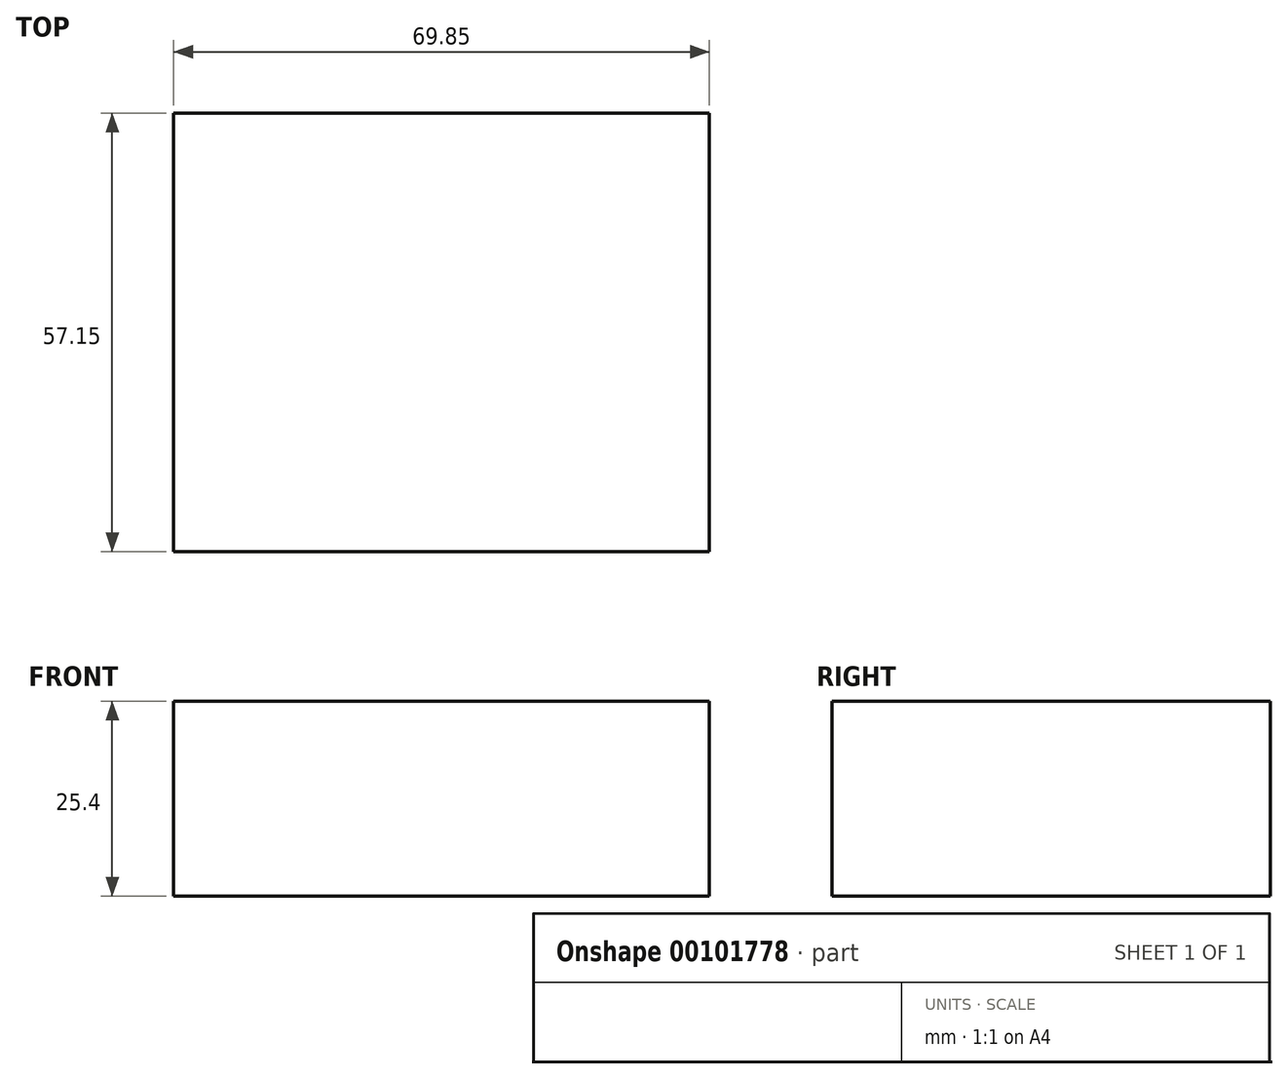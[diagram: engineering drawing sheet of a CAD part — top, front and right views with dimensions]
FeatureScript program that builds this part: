
annotation { "Feature Type Name" : "Feature", "Feature Type Description" : "" }
export const myFeature = defineFeature(function(context is Context, id is Id, definition is map)
    precondition{}
    {
        {
            var Q0;
            Q0=qCreatedBy(makeId("Front.planeOp"),FACE);
            var sketch = newSketch(context, id + "F0", { "sketchPlane" : qUnion([Q0])});
            skLineSegment(sketch, "E0.bottom", {"start": v(-23.12, 6.57) * mm, "end": v(46.73, 6.57) * mm});
            skLineSegment(sketch, "E0.top", {"start": v(-23.12, -18.83) * mm, "end": v(46.73, -18.83) * mm});
            skLineSegment(sketch, "E0.left", {"start": v(-23.12, 6.57) * mm, "end": v(-23.12, -18.83) * mm});
            skLineSegment(sketch, "E0.right", {"start": v(46.73, 6.57) * mm, "end": v(46.73, -18.83) * mm});
            skSolve(sketch);
        }
        {
            var Q0;
            Q0=makeQuery(id+"F0.imprint","IMPRINT",FACE,{"disambiguationData":[TD([[makeQuery(id+"F0.imprint","IMPRINT",EDGE,{"derivedFrom":sQuery(id+"F0.wireOp",EDGE,"E0.bottom")}),-1.0]])]});
            extrude(context, id + "F1", {"entities" : qUnion([Q0]), "depth" : 57.15 * mm});
        }
    });
